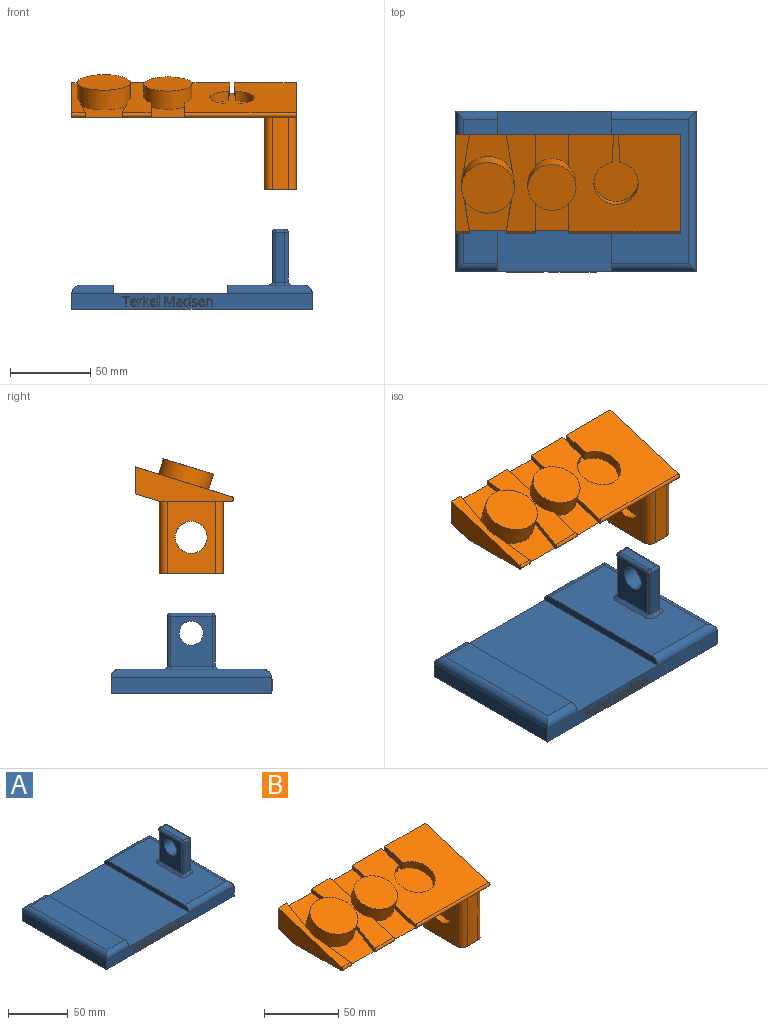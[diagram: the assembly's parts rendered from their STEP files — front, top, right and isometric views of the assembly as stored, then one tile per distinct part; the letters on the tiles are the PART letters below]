
ASSEMBLY  parts=2 mates=1
PART A: 267 faces, bbox 150x101x50 mm
  f0: plane 150x10mm, normal (0,-1,0), area 1389.4mm2, adj f3,f5,f6,f8,f17,f40,f41,f42
  f1: plane 90x48mm, normal (0,0,1), area 3857.7mm2, adj f2,f3,f16,f30,f31,f32,f33,f34
  f2: cylinder r=5mm len=53mm, axis (1,0,0), area 402mm2, adj f1,f4,f16,f39
  f3: cylinder r=5mm len=53mm, axis (-1,0,0), area 402mm2, adj f0,f1,f16,f39
  f4: plane 150x10mm, normal (0,1,0), area 1500mm2, adj f2,f5,f6,f8,f14,f40
  f5: plane 100x10mm, normal (-1,0,0), area 1000mm2, adj f0,f4,f8,f15
  f6: plane 100x10mm, normal (1,0,0), area 1000mm2, adj f0,f4,f8,f16
  f7: plane 90x21mm, normal (0,0,1), area 1890mm2, adj f14,f15,f17,f38
  f8: plane 150x100mm, normal (0,0,-1), area 15000mm2, adj f0,f4,f5,f6
  f9: plane 31x6mm, normal (0,1,0), area 186mm2, adj f20,f26,f29,f34
  f10: plane 31x26mm, normal (-1,0,0), area 629.3mm2, adj f23,f27,f29,f30,f266
  f11: plane 31x6mm, normal (0,-1,0), area 186mm2, adj f18,f22,f23,f33
  f12: plane 31x26mm, normal (1,0,0), area 629.3mm2, adj f18,f20,f21,f37,f266
  f13: plane 26x6mm, normal (0,0,1), area 156mm2, adj f21,f22,f26,f27
  f14: cylinder r=5mm len=26mm, axis (1,0,0), area 189.9mm2, adj f4,f7,f15,f38
  f15: cylinder r=5mm len=100mm, axis (0,1,0), area 756.9mm2, adj f5,f7,f14,f17
  f16: cylinder r=5mm len=100mm, axis (0,-1,0), area 756.9mm2, adj f1,f2,f3,f6
  f17: cylinder r=5mm len=26mm, axis (-1,0,0), area 189.9mm2, adj f0,f7,f15,f38
  f18: cylinder r=2mm len=31mm, axis (0,0,1), area 97.4mm2, adj f11,f12,f19,f35
  f19: sphere r=2mm, area 6.3mm2, adj f18,f21,f22
  f20: cylinder r=2mm len=31mm, axis (0,0,-1), area 97.4mm2, adj f9,f12,f24,f36
  f21: cylinder r=2mm len=26mm, axis (0,-1,0), area 81.7mm2, adj f12,f13,f19,f24
  f22: cylinder r=2mm len=6mm, axis (-1,0,0), area 18.8mm2, adj f11,f13,f19,f25
  f23: cylinder r=2mm len=31mm, axis (0,0,-1), area 97.4mm2, adj f10,f11,f25,f31
  f24: sphere r=2mm, area 6.3mm2, adj f20,f21,f26
  f25: sphere r=2mm, area 6.3mm2, adj f22,f23,f27
  f26: cylinder r=2mm len=6mm, axis (1,0,0), area 18.8mm2, adj f9,f13,f24,f28
  f27: cylinder r=2mm len=26mm, axis (0,1,0), area 81.7mm2, adj f10,f13,f25,f28
  f28: sphere r=2mm, area 6.3mm2, adj f26,f27,f29
  f29: cylinder r=2mm len=31mm, axis (0,0,1), area 97.4mm2, adj f9,f10,f28,f32
  f30: plane 26x2mm, normal (-0.71,0,0.71), area 73.5mm2, adj f1,f10,f31,f32
  f31: cone r=4mm half-angle=45deg, axis (0,0,-1), area 13.3mm2, adj f1,f23,f30,f33
  f32: cone r=4mm half-angle=45deg, axis (0,0,-1), area 13.3mm2, adj f1,f29,f30,f34
  f33: plane 6x2mm, normal (0,-0.71,0.71), area 17mm2, adj f1,f11,f31,f35
  f34: plane 6x2mm, normal (0,0.71,0.71), area 17mm2, adj f1,f9,f32,f36
  f35: cone r=4mm half-angle=45deg, axis (0,0,-1), area 13.3mm2, adj f1,f18,f33,f37
  f36: cone r=4mm half-angle=45deg, axis (0,0,-1), area 13.3mm2, adj f1,f20,f34,f37
  f37: plane 26x2mm, normal (0.71,0,0.71), area 73.5mm2, adj f1,f12,f35,f36
  f38: plane 100x5mm, normal (1,0,0), area 489.3mm2, adj f7,f14,f17,f40
  f39: plane 100x5mm, normal (-1,0,0), area 489.3mm2, adj f1,f2,f3,f40
  f40: plane 100x71mm, normal (0,0,1), area 7100mm2, adj f0,f4,f38,f39
  f41: plane 1x0.69mm, normal (0,0,-1), area 0.7mm2, adj f0,f42,f48,f49
  f42: plane 5.33x1mm, normal (1,0,0), area 5.3mm2, adj f0,f41,f43,f49
  f43: plane 1.88x1mm, normal (0,0,-1), area 1.9mm2, adj f0,f42,f44,f49
  f44: plane 1x0.61mm, normal (1,0,0), area 0.6mm2, adj f0,f43,f45,f49
  f45: plane 4.46x1mm, normal (0,0,1), area 4.5mm2, adj f0,f44,f46,f49
  f46: plane 1x0.61mm, normal (-1,0,0), area 0.6mm2, adj f0,f45,f47,f49
  f47: plane 1.88x1mm, normal (0,0,-1), area 1.9mm2, adj f0,f46,f48,f49
  f48: plane 5.33x1mm, normal (-1,0,0), area 5.3mm2, adj f0,f41,f47,f49
  f49: plane 5.95x4.46mm, normal (0,-1,0), area 6.4mm2, adj f41,f42,f43,f44,f45,f46,f47,f48
  f50: extruded ~1x0.86mm, area 1mm2, adj f51,f68,f69,f70
  f51: extruded ~1x0.81mm, area 0.9mm2, adj f50,f52,f69,f70
  f52: extruded ~1x0.98mm, area 1mm2, adj f51,f53,f69,f70
  f53: plane 2.33x1mm, normal (0,0,1), area 2.3mm2, adj f52,f68,f69,f70
  f54: extruded ~1.56x1mm, area 1.7mm2, adj f0,f55,f67,f69
  f55: extruded ~1x0.77mm, area 0.8mm2, adj f0,f54,f56,f69
  f56: extruded ~1x0.68mm, area 0.7mm2, adj f0,f55,f57,f69
  f57: plane 1x0.6mm, normal (1,0,0), area 0.6mm2, adj f0,f56,f58,f69
  f58: extruded ~1.42x1mm, area 1.5mm2, adj f0,f57,f59,f69
  f59: extruded ~1.06x1mm, area 1.2mm2, adj f0,f58,f60,f69
  f60: extruded ~1.19x1mm, area 1.3mm2, adj f0,f59,f61,f69
  f61: plane 3.07x1mm, normal (0,0,-1), area 3.1mm2, adj f0,f60,f62,f69
  f62: plane 1x0.43mm, normal (1,0,0), area 0.4mm2, adj f0,f61,f63,f69
  f63: extruded ~1.46x1mm, area 1.6mm2, adj f0,f62,f64,f69
  f64: extruded ~1.33x1mm, area 1.5mm2, adj f0,f63,f65,f69
  f65: extruded ~1.43x1mm, area 1.6mm2, adj f0,f64,f66,f69
  f66: extruded ~1.71x1mm, area 1.8mm2, adj f0,f65,f67,f69
  f67: extruded ~1.67x1mm, area 1.8mm2, adj f0,f54,f66,f69
  f68: extruded ~1x0.97mm, area 1.1mm2, adj f50,f53,f69,f70
  f69: plane 4.62x3.77mm, normal (0,-1,0), area 7.9mm2, adj f50,f51,f52,f53,f54,f55,f56,f57
  f70: plane 2.33x1.32mm, normal (0,-1,0), area 2.5mm2, adj f50,f51,f52,f53,f68
  f71: extruded ~1x0.53mm, area 0.5mm2, adj f0,f72,f83,f84
  f72: extruded ~1x0.77mm, area 0.8mm2, adj f0,f71,f73,f84
  f73: extruded ~1x0.67mm, area 0.9mm2, adj f0,f72,f74,f84
  f74: plane 1x0.03mm, normal (0,0,1), area 0mm2, adj f0,f73,f75,f84
  f75: plane 1x0.83mm, normal (1,0,0.09), area 0.8mm2, adj f0,f74,f76,f84
  f76: plane 1x0.56mm, normal (0,0,1), area 0.6mm2, adj f0,f75,f77,f84
  f77: plane 4.46x1mm, normal (-1,0,0), area 4.5mm2, adj f0,f76,f78,f84
  f78: plane 1x0.68mm, normal (0,0,-1), area 0.7mm2, adj f0,f77,f79,f84
  f79: plane 2.39x1mm, normal (1,0,0), area 2.4mm2, adj f0,f78,f80,f84
  f80: extruded ~1.09x1mm, area 1.2mm2, adj f0,f79,f81,f84
  f81: extruded ~1x0.93mm, area 1.1mm2, adj f0,f80,f82,f84
  f82: extruded ~1x0.49mm, area 0.5mm2, adj f0,f81,f83,f84
  f83: plane 1x0.63mm, normal (0.99,0,-0.15), area 0.6mm2, adj f0,f71,f82,f84
  f84: plane 4.54x2.57mm, normal (0,-1,0), area 4.1mm2, adj f71,f72,f73,f74,f75,f76,f77,f78
  f85: extruded ~1x0.65mm, area 0.8mm2, adj f0,f86,f99,f100
  f86: plane 1x0.03mm, normal (0,0,1), area 0mm2, adj f0,f85,f87,f100
  f87: extruded ~1x0.69mm, area 0.7mm2, adj f0,f86,f88,f100
  f88: plane 3.36x1mm, normal (1,0,0), area 3.4mm2, adj f0,f87,f89,f100
  f89: plane 1x0.67mm, normal (0,0,1), area 0.7mm2, adj f0,f88,f90,f100
  f90: plane 6.33x1mm, normal (-1,0,0), area 6.3mm2, adj f0,f89,f91,f100
  f91: plane 1x0.67mm, normal (0,0,-1), area 0.7mm2, adj f0,f90,f92,f100
  f92: plane 1.67x1mm, normal (1,0,0), area 1.7mm2, adj f0,f91,f93,f100
  f93: plane 1x0.51mm, normal (0.65,0,-0.76), area 0.7mm2, adj f0,f92,f94,f100
  f94: plane 2.11x1.58mm, normal (-0.8,0,-0.6), area 2.6mm2, adj f0,f93,f95,f100
  f95: plane 1x0.82mm, normal (0,0,-1), area 0.8mm2, adj f0,f94,f96,f100
  f96: plane 2.56x1.93mm, normal (0.8,0,0.6), area 3.2mm2, adj f0,f95,f97,f100
  f97: plane 1.9x1.81mm, normal (0.72,0,-0.69), area 2.6mm2, adj f0,f96,f98,f100
  f98: plane 1x0.8mm, normal (0,0,1), area 0.8mm2, adj f0,f97,f99,f100
  f99: plane 1.53x1.44mm, normal (-0.73,0,0.69), area 2.1mm2, adj f0,f85,f98,f100
  f100: plane 6.33x3.57mm, normal (0,-1,0), area 8mm2, adj f85,f86,f87,f88,f89,f90,f91,f92
  f101: extruded ~1x0.86mm, area 1mm2, adj f102,f119,f120,f121
  f102: extruded ~1x0.81mm, area 0.9mm2, adj f101,f103,f120,f121
  f103: extruded ~1x0.98mm, area 1mm2, adj f102,f104,f120,f121
  f104: plane 2.33x1mm, normal (0,0,1), area 2.3mm2, adj f103,f119,f120,f121
  f105: extruded ~1.56x1mm, area 1.7mm2, adj f0,f106,f118,f120
  f106: extruded ~1x0.77mm, area 0.8mm2, adj f0,f105,f107,f120
  f107: extruded ~1x0.68mm, area 0.7mm2, adj f0,f106,f108,f120
  f108: plane 1x0.6mm, normal (1,0,0), area 0.6mm2, adj f0,f107,f109,f120
  f109: extruded ~1.42x1mm, area 1.5mm2, adj f0,f108,f110,f120
  f110: extruded ~1.06x1mm, area 1.2mm2, adj f0,f109,f111,f120
  f111: extruded ~1.19x1mm, area 1.3mm2, adj f0,f110,f112,f120
  f112: plane 3.07x1mm, normal (0,0,-1), area 3.1mm2, adj f0,f111,f113,f120
  f113: plane 1x0.43mm, normal (1,0,0), area 0.4mm2, adj f0,f112,f114,f120
  f114: extruded ~1.46x1mm, area 1.6mm2, adj f0,f113,f115,f120
  f115: extruded ~1.33x1mm, area 1.5mm2, adj f0,f114,f116,f120
  f116: extruded ~1.43x1mm, area 1.6mm2, adj f0,f115,f117,f120
  f117: extruded ~1.71x1mm, area 1.8mm2, adj f0,f116,f118,f120
  f118: extruded ~1.67x1mm, area 1.8mm2, adj f0,f105,f117,f120
  f119: extruded ~1x0.97mm, area 1.1mm2, adj f101,f104,f120,f121
  f120: plane 4.62x3.77mm, normal (0,-1,0), area 7.9mm2, adj f101,f102,f103,f104,f105,f106,f107,f108
  f121: plane 2.33x1.32mm, normal (0,-1,0), area 2.5mm2, adj f101,f102,f103,f104,f119
  f122: plane 1x0.68mm, normal (0,0,-1), area 0.7mm2, adj f0,f123,f125,f126
  f123: plane 6.33x1mm, normal (1,0,0), area 6.3mm2, adj f0,f122,f124,f126
  f124: plane 1x0.68mm, normal (0,0,1), area 0.7mm2, adj f0,f123,f125,f126
  f125: plane 6.33x1mm, normal (-1,0,0), area 6.3mm2, adj f0,f122,f124,f126
  f126: plane 6.33x0.68mm, normal (0,-1,0), area 4.3mm2, adj f122,f123,f124,f125
  f127: plane 5.27x2.02mm, normal (-0.93,0,-0.36), area 5.6mm2, adj f0,f128,f144,f145
  f128: plane 1x0.56mm, normal (0,0,-1), area 0.6mm2, adj f0,f127,f129,f145
  f129: plane 5.27x2.04mm, normal (0.93,0,-0.36), area 5.6mm2, adj f0,f128,f130,f145
  f130: plane 1x0.03mm, normal (0,0,-1), area 0mm2, adj f0,f129,f131,f145
  f131: extruded ~1.43x1mm, area 1.4mm2, adj f0,f130,f132,f145
  f132: plane 3.83x1mm, normal (-1,0,0), area 3.8mm2, adj f0,f131,f133,f145
  f133: plane 1x0.69mm, normal (0,0,-1), area 0.7mm2, adj f0,f132,f134,f145
  f134: plane 5.95x1mm, normal (1,0,0), area 5.9mm2, adj f0,f133,f135,f145
  f135: plane 1.03x1mm, normal (0,0,1), area 1mm2, adj f0,f134,f136,f145
  f136: plane 4.91x1.9mm, normal (-0.93,0,0.36), area 5.3mm2, adj f0,f135,f137,f145
  f137: plane 1x0.03mm, normal (0,0,1), area 0mm2, adj f0,f136,f138,f145
  f138: plane 4.91x1.88mm, normal (0.93,0,0.36), area 5.3mm2, adj f0,f137,f139,f145
  f139: plane 1.04x1mm, normal (0,0,1), area 1mm2, adj f0,f138,f140,f145
  f140: plane 5.95x1mm, normal (-1,0,0), area 5.9mm2, adj f0,f139,f141,f145
  f141: plane 1x0.64mm, normal (0,0,-1), area 0.6mm2, adj f0,f140,f142,f145
  f142: plane 3.78x1mm, normal (1,0,0), area 3.8mm2, adj f0,f141,f143,f145
  f143: extruded ~1.49x1mm, area 1.5mm2, adj f0,f142,f144,f145
  f144: plane 1x0.03mm, normal (0,0,-1), area 0mm2, adj f0,f127,f143,f145
  f145: plane 5.95x5.89mm, normal (0,-1,0), area 15.1mm2, adj f127,f128,f129,f130,f131,f132,f133,f134
  f146: extruded ~1x0.99mm, area 1.1mm2, adj f147,f172,f173,f174
  f147: extruded ~1x0.62mm, area 0.7mm2, adj f146,f148,f173,f174
  f148: extruded ~1x0.56mm, area 0.6mm2, adj f147,f149,f173,f174
  f149: extruded ~1x0.69mm, area 0.8mm2, adj f148,f150,f173,f174
  f150: extruded ~1.16x1mm, area 1.2mm2, adj f149,f151,f173,f174
  f151: plane 1x0.68mm, normal (0.04,0,-1), area 0.7mm2, adj f150,f152,f173,f174
  f152: plane 1x0.4mm, normal (-1,0,0), area 0.4mm2, adj f151,f172,f173,f174
  f153: plane 1x0.64mm, normal (-0.98,0,-0.21), area 0.6mm2, adj f0,f154,f171,f173
  f154: plane 1x0.5mm, normal (0,0,-1), area 0.5mm2, adj f0,f153,f155,f173
  f155: plane 3.04x1mm, normal (1,0,0), area 3mm2, adj f0,f154,f156,f173
  f156: extruded ~1.13x1mm, area 1.2mm2, adj f0,f155,f157,f173
  f157: extruded ~1.18x1mm, area 1.3mm2, adj f0,f156,f158,f173
  f158: extruded ~1x0.79mm, area 0.8mm2, adj f0,f157,f159,f173
  f159: extruded ~1x0.72mm, area 0.8mm2, adj f0,f158,f160,f173
  f160: plane 1x0.52mm, normal (-0.93,0,-0.37), area 0.6mm2, adj f0,f159,f161,f173
  f161: extruded ~1.26x1mm, area 1.3mm2, adj f0,f160,f162,f173
  f162: extruded ~1x0.72mm, area 0.8mm2, adj f0,f161,f163,f173
  f163: extruded ~1x0.77mm, area 0.8mm2, adj f0,f162,f164,f173
  f164: plane 1x0.28mm, normal (-1,0,0), area 0.3mm2, adj f0,f163,f165,f173
  f165: plane 1x0.76mm, normal (-0.03,0,1), area 0.8mm2, adj f0,f164,f166,f173
  f166: extruded ~2.16x1.42mm, area 2.9mm2, adj f0,f165,f167,f173
  f167: extruded ~1x0.97mm, area 1.1mm2, adj f0,f166,f168,f173
  f168: extruded ~1.04x1mm, area 1.1mm2, adj f0,f167,f169,f173
  f169: extruded ~1x0.83mm, area 0.8mm2, adj f0,f168,f170,f173
  f170: extruded ~1x0.66mm, area 0.9mm2, adj f0,f169,f171,f173
  f171: plane 1x0.03mm, normal (0,0,-1), area 0mm2, adj f0,f153,f170,f173
  f172: extruded ~1x0.97mm, area 1.1mm2, adj f146,f152,f173,f174
  f173: plane 4.61x3.58mm, normal (0,-1,0), area 7.8mm2, adj f146,f147,f148,f149,f150,f151,f152,f153
  f174: plane 2.19x1.72mm, normal (0,-1,0), area 3mm2, adj f146,f147,f148,f149,f150,f151,f152,f172
  f175: extruded ~1x1mm, area 1.1mm2, adj f176,f198,f199,f200
  f176: extruded ~1x0.92mm, area 1.1mm2, adj f175,f177,f199,f200
  f177: extruded ~1.29x1mm, area 1.3mm2, adj f176,f178,f199,f200
  f178: extruded ~1.3x1mm, area 1.4mm2, adj f177,f179,f199,f200
  f179: extruded ~1x0.91mm, area 1.1mm2, adj f178,f180,f199,f200
  f180: extruded ~1.01x1mm, area 1.1mm2, adj f179,f181,f199,f200
  f181: extruded ~1.35x1mm, area 1.4mm2, adj f180,f182,f199,f200
  f182: plane 1x0.14mm, normal (-1,0,0), area 0.1mm2, adj f181,f198,f199,f200
  f183: plane 1x0.04mm, normal (0,0,-1), area 0mm2, adj f0,f184,f197,f199
  f184: plane 1x0.6mm, normal (-0.99,0,-0.15), area 0.6mm2, adj f0,f183,f185,f199
  f185: plane 1x0.55mm, normal (0,0,-1), area 0.5mm2, adj f0,f184,f186,f199
  f186: plane 6.33x1mm, normal (1,0,0), area 6.3mm2, adj f0,f185,f187,f199
  f187: plane 1x0.68mm, normal (0,0,1), area 0.7mm2, adj f0,f186,f188,f199
  f188: plane 1.82x1mm, normal (-1,0,0), area 1.8mm2, adj f0,f187,f189,f199
  f189: plane 1x0.31mm, normal (-1,0,-0.05), area 0.3mm2, adj f0,f188,f190,f199
  f190: plane 1x0.32mm, normal (-1,0,-0.09), area 0.3mm2, adj f0,f189,f191,f199
  f191: plane 1x0.05mm, normal (0,0,1), area 0.1mm2, adj f0,f190,f192,f199
  f192: extruded ~1.39x1mm, area 1.6mm2, adj f0,f191,f193,f199
  f193: extruded ~1.36x1mm, area 1.5mm2, adj f0,f192,f194,f199
  f194: extruded ~1.71x1mm, area 1.8mm2, adj f0,f193,f195,f199
  f195: extruded ~1.7x1mm, area 1.8mm2, adj f0,f194,f196,f199
  f196: extruded ~1.36x1mm, area 1.5mm2, adj f0,f195,f197,f199
  f197: extruded ~1.4x1mm, area 1.6mm2, adj f0,f183,f196,f199
  f198: extruded ~1.22x1mm, area 1.3mm2, adj f175,f182,f199,f200
  f199: plane 6.41x3.92mm, normal (0,-1,0), area 9.7mm2, adj f175,f176,f177,f178,f179,f180,f181,f182
  f200: plane 3.49x2.55mm, normal (0,-1,0), area 7.5mm2, adj f175,f176,f177,f178,f179,f180,f181,f182
  f201: extruded ~1x0.96mm, area 1.1mm2, adj f0,f202,f225,f226
  f202: extruded ~1x0.74mm, area 0.8mm2, adj f0,f201,f203,f226
  f203: extruded ~1.07x1mm, area 1.2mm2, adj f0,f202,f204,f226
  f204: extruded ~1x0.78mm, area 0.8mm2, adj f0,f203,f205,f226
  f205: extruded ~1x0.3mm, area 0.4mm2, adj f0,f204,f206,f226
  f206: extruded ~1x0.31mm, area 0.3mm2, adj f0,f205,f207,f226
  f207: extruded ~1x0.41mm, area 0.5mm2, adj f0,f206,f208,f226
  f208: extruded ~1x0.72mm, area 0.7mm2, adj f0,f207,f209,f226
  f209: extruded ~1.22x1mm, area 1.3mm2, adj f0,f208,f210,f226
  f210: plane 1x0.55mm, normal (0.92,0,-0.4), area 0.6mm2, adj f0,f209,f211,f226
  f211: extruded ~1.41x1mm, area 1.4mm2, adj f0,f210,f212,f226
  f212: extruded ~1.22x1mm, area 1.3mm2, adj f0,f211,f213,f226
  f213: extruded ~1x0.86mm, area 1mm2, adj f0,f212,f214,f226
  f214: extruded ~1x0.52mm, area 0.5mm2, adj f0,f213,f215,f226
  f215: extruded ~1x0.39mm, area 0.6mm2, adj f0,f214,f216,f226
  f216: extruded ~1x0.88mm, area 1mm2, adj f0,f215,f217,f226
  f217: extruded ~1x0.88mm, area 1mm2, adj f0,f216,f218,f226
  f218: extruded ~1x0.45mm, area 0.5mm2, adj f0,f217,f219,f226
  f219: extruded ~1x0.52mm, area 0.6mm2, adj f0,f218,f220,f226
  f220: extruded ~1x0.81mm, area 0.8mm2, adj f0,f219,f221,f226
  f221: extruded ~1x0.71mm, area 0.7mm2, adj f0,f220,f222,f226
  f222: extruded ~1x0.69mm, area 0.7mm2, adj f0,f221,f223,f226
  f223: plane 1x0.63mm, normal (-1,0,0), area 0.6mm2, adj f0,f222,f224,f226
  f224: extruded ~1.38x1mm, area 1.4mm2, adj f0,f223,f225,f226
  f225: extruded ~1.3x1mm, area 1.4mm2, adj f0,f201,f224,f226
  f226: plane 4.62x3.16mm, normal (0,-1,0), area 6.1mm2, adj f201,f202,f203,f204,f205,f206,f207,f208
  f227: extruded ~1x0.86mm, area 1mm2, adj f228,f245,f246,f247
  f228: extruded ~1x0.81mm, area 0.9mm2, adj f227,f229,f246,f247
  f229: extruded ~1x0.98mm, area 1mm2, adj f228,f230,f246,f247
  f230: plane 2.33x1mm, normal (0,0,1), area 2.3mm2, adj f229,f245,f246,f247
  f231: extruded ~1.56x1mm, area 1.7mm2, adj f0,f232,f244,f246
  f232: extruded ~1x0.77mm, area 0.8mm2, adj f0,f231,f233,f246
  f233: extruded ~1x0.68mm, area 0.7mm2, adj f0,f232,f234,f246
  f234: plane 1x0.6mm, normal (1,0,0), area 0.6mm2, adj f0,f233,f235,f246
  f235: extruded ~1.42x1mm, area 1.5mm2, adj f0,f234,f236,f246
  f236: extruded ~1.06x1mm, area 1.2mm2, adj f0,f235,f237,f246
  f237: extruded ~1.19x1mm, area 1.3mm2, adj f0,f236,f238,f246
  f238: plane 3.07x1mm, normal (0,0,-1), area 3.1mm2, adj f0,f237,f239,f246
  f239: plane 1x0.43mm, normal (1,0,0), area 0.4mm2, adj f0,f238,f240,f246
  f240: extruded ~1.46x1mm, area 1.6mm2, adj f0,f239,f241,f246
  f241: extruded ~1.33x1mm, area 1.5mm2, adj f0,f240,f242,f246
  f242: extruded ~1.43x1mm, area 1.6mm2, adj f0,f241,f243,f246
  f243: extruded ~1.71x1mm, area 1.8mm2, adj f0,f242,f244,f246
  f244: extruded ~1.67x1mm, area 1.8mm2, adj f0,f231,f243,f246
  f245: extruded ~1x0.97mm, area 1.1mm2, adj f227,f230,f246,f247
  f246: plane 4.62x3.77mm, normal (0,-1,0), area 7.9mm2, adj f227,f228,f229,f230,f231,f232,f233,f234
  f247: plane 2.33x1.32mm, normal (0,-1,0), area 2.5mm2, adj f227,f228,f229,f230,f245
  f248: plane 2.89x1mm, normal (-1,0,0), area 2.9mm2, adj f0,f249,f264,f265
  f249: plane 1x0.68mm, normal (0,0,-1), area 0.7mm2, adj f0,f248,f250,f265
  f250: plane 2.91x1mm, normal (1,0,0), area 2.9mm2, adj f0,f249,f251,f265
  f251: extruded ~1.24x1mm, area 1.3mm2, adj f0,f250,f252,f265
  f252: extruded ~1.21x1mm, area 1.3mm2, adj f0,f251,f253,f265
  f253: extruded ~1x0.83mm, area 0.9mm2, adj f0,f252,f254,f265
  f254: extruded ~1x0.58mm, area 0.8mm2, adj f0,f253,f255,f265
  f255: plane 1x0.03mm, normal (0,0,1), area 0mm2, adj f0,f254,f256,f265
  f256: plane 1x0.61mm, normal (0.98,0,0.18), area 0.6mm2, adj f0,f255,f257,f265
  f257: plane 1x0.55mm, normal (0,0,1), area 0.5mm2, adj f0,f256,f258,f265
  f258: plane 4.46x1mm, normal (-1,0,0), area 4.5mm2, adj f0,f257,f259,f265
  f259: plane 1x0.68mm, normal (0,0,-1), area 0.7mm2, adj f0,f258,f260,f265
  f260: plane 2.34x1mm, normal (1,0,0), area 2.3mm2, adj f0,f259,f261,f265
  f261: extruded ~1.25x1mm, area 1.3mm2, adj f0,f260,f262,f265
  f262: extruded ~1.02x1mm, area 1.1mm2, adj f0,f261,f263,f265
  f263: extruded ~1x0.78mm, area 0.8mm2, adj f0,f262,f264,f265
  f264: extruded ~1x0.81mm, area 0.9mm2, adj f0,f248,f263,f265
  f265: plane 4.54x3.73mm, normal (0,-1,0), area 7.2mm2, adj f248,f249,f250,f251,f252,f253,f254,f255
  f266: cylinder r=7.5mm len=15mm, axis (1,0,0), area 471.2mm2, adj f10,f12
PART B: 60 faces, bbox 140x61.5x71.6 mm
  f0: plane 140x16.88mm, normal (0,1,0), area 1951.2mm2, adj f1,f4,f5,f9,f19,f21,f25,f28
  f1: plane 66.48x61.5mm, normal (1,0,0), area 1736.3mm2, adj f0,f6,f8,f9,f10,f20,f21,f30
  f2: plane 8.02x6.51mm, normal (-1,0,0), area 27.8mm2, adj f6,f9,f24,f28,f57,f58,f59
  f3: cylinder r=1.5mm len=18mm, axis (1,0,0), area 76.8mm2, adj f4,f8,f41,f51
  f4: plane 60.44x18.55mm, normal (0,-0.29,0.96), area 912.1mm2, adj f0,f3,f39,f41,f45,f47,f52,f55
  f5: plane 60.44x18.55mm, normal (0,-0.29,0.96), area 377.9mm2, adj f0,f7,f19,f47,f49,f54
  f6: plane 38.5x3.59mm, normal (0,1,0), area 138.2mm2, adj f1,f2,f9,f58
  f7: cylinder r=1.5mm len=8.5mm, axis (1,0,0), area 36.3mm2, adj f5,f8,f19,f50
  f8: plane 140x45mm, normal (0,0,-1), area 5506.2mm2, adj f1,f3,f7,f13,f14,f19,f20,f21
  f9: plane 69.5x60.44mm, normal (0,-0.29,0.96), area 3660.4mm2, adj f0,f1,f2,f6,f20,f22,f23,f24
  f10: plane 40x20mm, normal (0,0,-1), area 302.5mm2, adj f1,f12,f13,f14,f29,f30,f31,f32
  f11: plane 33x10mm, normal (0,-1,0), area 330mm2, adj f15,f17,f18,f36
  f12: plane 45x10mm, normal (0,1,0), area 450mm2, adj f10,f21,f31,f32
  f13: plane 45x10mm, normal (0,-1,0), area 450mm2, adj f8,f10,f29,f30
  f14: plane 45x30mm, normal (-1,0,0), area 1035.8mm2, adj f8,f10,f29,f31,f37
  f15: plane 33x30mm, normal (-1,0,0), area 675.8mm2, adj f11,f16,f18,f34,f38
  f16: plane 33x10mm, normal (0,1,0), area 330mm2, adj f15,f17,f18,f33
  f17: plane 33x30mm, normal (1,0,0), area 675.8mm2, adj f11,f16,f18,f35,f37
  f18: plane 30x10mm, normal (0,0,-1), area 300mm2, adj f11,f15,f16,f17
  f19: plane 61.5x21.48mm, normal (-1,0,0), area 705.6mm2, adj f0,f5,f7,f8,f21
  f20: cylinder r=1.5mm len=69.5mm, axis (1,0,0), area 296.5mm2, adj f1,f8,f9,f42
  f21: plane 140x20mm, normal (0,0.29,-0.96), area 2202.3mm2, adj f0,f1,f8,f12,f19,f32
  f22: cylinder r=13.85mm len=28.19mm, axis (0,-0.29,0.96), area 523mm2, adj f9,f23,f27,f28
  f23: plane 12.46x9.28mm, normal (-1,0,0), area 69.9mm2, adj f9,f22,f24,f28
  f24: plane 6.02x1.85mm, normal (0,-0.96,-0.29), area 3.2mm2, adj f2,f9,f23,f28
  f25: plane 8.02x6.51mm, normal (1,0,0), area 36.8mm2, adj f0,f9,f26,f28
  f26: plane 6.02x1.85mm, normal (0,-0.96,-0.29), area 3.2mm2, adj f9,f25,f27,f28
  f27: plane 12.46x9.28mm, normal (1,0,0), area 69.9mm2, adj f9,f22,f26,f28
  f28: plane 41.61x27.7mm, normal (0,-0.29,0.96), area 661.3mm2, adj f0,f2,f22,f23,f24,f25,f26,f27
  f29: cylinder r=5mm len=45mm, axis (0,0,1), area 353.4mm2, adj f8,f10,f13,f14
  f30: cylinder r=5mm len=45mm, axis (0,0,1), area 353.4mm2, adj f1,f8,f10,f13
  f31: cylinder r=5mm len=45mm, axis (0,0,1), area 353.4mm2, adj f8,f10,f12,f14
  f32: cylinder r=5mm len=45mm, axis (0,0,1), area 349mm2, adj f1,f10,f12,f21
  f33: plane 14x2mm, normal (0,0.71,-0.71), area 33.9mm2, adj f10,f16,f34,f35
  f34: plane 34x2mm, normal (-0.71,0,-0.71), area 90.5mm2, adj f10,f15,f33,f36
  f35: plane 34x2mm, normal (0.71,0,-0.71), area 90.5mm2, adj f10,f17,f33,f36
  f36: plane 14x2mm, normal (0,-0.71,-0.71), area 33.9mm2, adj f10,f11,f34,f35
  f37: cylinder r=10mm len=20mm, axis (1,0,0), area 314.2mm2, adj f14,f17
  f38: cylinder r=10mm len=20mm, axis (1,0,0), area 314.2mm2, adj f1,f15
  f39: cylinder r=15mm len=32.2mm, axis (0,0.29,-0.96), area 987.8mm2, adj f4,f9,f40,f41,f42,f43,f44,f45
  f40: plane 30x28.68mm, normal (0,-0.29,0.96), area 706.9mm2, adj f39
  f41: plane 21.92x9.07mm, normal (1,0,0), area 66.2mm2, adj f3,f4,f8,f39,f43
  f42: plane 21.92x9.07mm, normal (-1,0,0), area 66.2mm2, adj f8,f9,f20,f39,f43
  f43: plane 21x20.19mm, normal (0,-0.29,0.96), area 381.6mm2, adj f8,f39,f41,f42
  f44: plane 19.98x9mm, normal (-1,0,0), area 61.3mm2, adj f0,f9,f39,f46
  f45: plane 19.98x9mm, normal (1,0,0), area 61.3mm2, adj f0,f4,f39,f46
  f46: plane 21x19.1mm, normal (0,-0.29,0.96), area 357.6mm2, adj f0,f39,f44,f45
  f47: cylinder r=16.5mm len=35.36mm, axis (0,0.29,-0.96), area 1285.6mm2, adj f4,f5,f48,f49,f52,f53,f54,f55
  f48: plane 33x31.55mm, normal (0,-0.29,0.96), area 855.3mm2, adj f47
  f49: plane 26.23x10.65mm, normal (0.99,0.15,0.05), area 80.5mm2, adj f5,f47,f50,f53
  f50: plane 2.93x1.94mm, normal (1,0,0), area 3.5mm2, adj f7,f8,f49,f53
  f51: plane 2.93x1.94mm, normal (-1,0,0), area 3.5mm2, adj f3,f8,f52,f53
  f52: plane 26.23x10.65mm, normal (-0.99,0.15,0.05), area 80.5mm2, adj f4,f47,f51,f53
  f53: plane 31.39x25.57mm, normal (0,-0.29,0.96), area 464mm2, adj f8,f47,f49,f50,f51,f52
  f54: plane 25.35x10.65mm, normal (0.99,-0.15,-0.05), area 79.1mm2, adj f0,f5,f47,f56
  f55: plane 25.35x10.65mm, normal (-0.99,-0.15,-0.05), area 79.1mm2, adj f0,f4,f47,f56
  f56: plane 31.39x24.47mm, normal (0,-0.29,0.96), area 437.5mm2, adj f0,f47,f54,f55
  f57: plane 38.5x3mm, normal (0,0,1), area 115.5mm2, adj f0,f1,f2,f59
  f58: plane 38.5x3mm, normal (0,0,-1), area 115.5mm2, adj f1,f2,f6,f59
  f59: plane 38.5x3mm, normal (0,1,0), area 115.5mm2, adj f1,f2,f57,f58
PLACE A t=(34.9,77.64,167.91)mm fixed
PLACE B t=(34.9,77.64,227.71)mm
MATE slider A.f13 <-> B.f18  axis (0,0,1) through (89.9,77.64,217.91)mm
